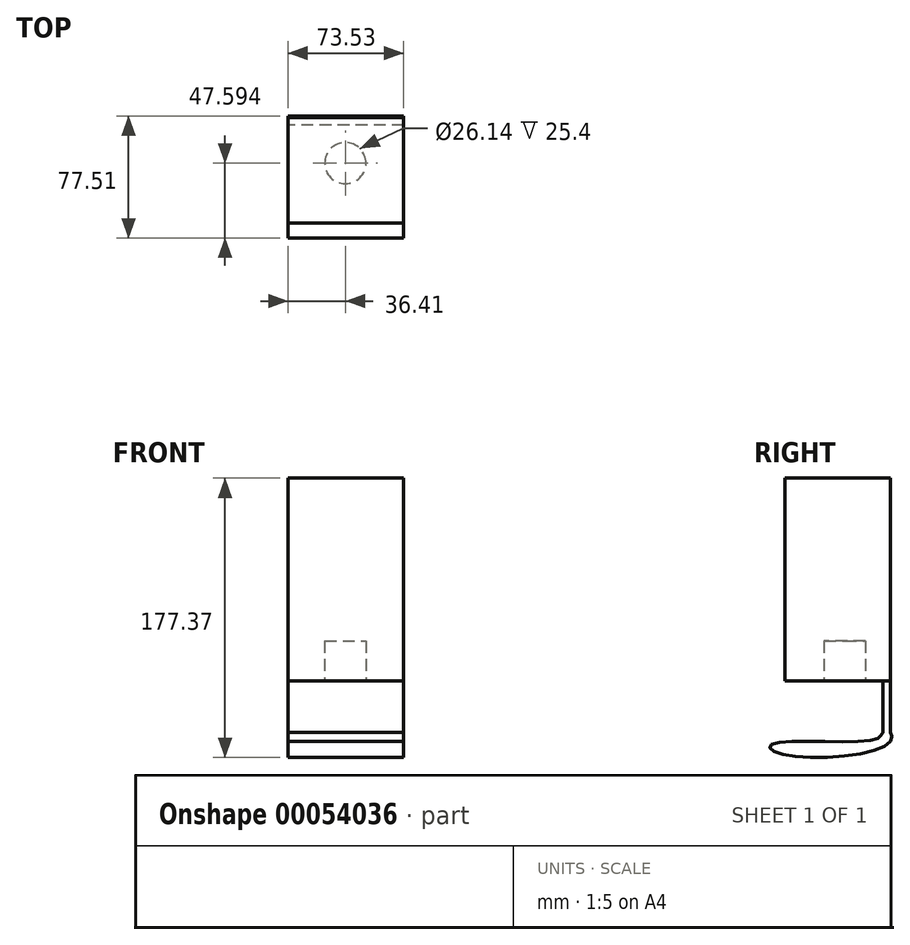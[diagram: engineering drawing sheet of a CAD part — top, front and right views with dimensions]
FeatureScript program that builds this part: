
annotation { "Feature Type Name" : "Feature", "Feature Type Description" : "" }
export const myFeature = defineFeature(function(context is Context, id is Id, definition is map)
    precondition{}
    {
        {
            var Q0;
            Q0=qCreatedBy(makeId("Front.planeOp"),FACE);
            var sketch = newSketch(context, id + "F0", { "sketchPlane" : qUnion([Q0])});
            skLineSegment(sketch, "E0.bottom", {"start": v(-36.41, 53.04) * mm, "end": v(37.08, 53.04) * mm});
            skLineSegment(sketch, "E0.top", {"start": v(-36.41, -75.77) * mm, "end": v(37.08, -75.77) * mm});
            skLineSegment(sketch, "E0.left", {"start": v(-36.41, 53.04) * mm, "end": v(-36.41, -75.77) * mm});
            skLineSegment(sketch, "E0.right", {"start": v(37.08, 53.04) * mm, "end": v(37.08, -75.77) * mm});
            skSolve(sketch);
        }
        {
            var Q0;
            Q0=makeQuery(id+"F0.imprint","IMPRINT",FACE,{"disambiguationData":[TD([[makeQuery(id+"F0.imprint","IMPRINT",EDGE,{"derivedFrom":sQuery(id+"F0.wireOp",EDGE,"E0.bottom")}),-1.0]])]});
            extrude(context, id + "F1", {"entities" : qUnion([Q0]), "depth" : 66.9 * mm});
        }
        {
            var Q0;
            Q0=makeQuery(id+"F1.opExtrude","SWEPT_FACE",FACE,{"disambiguationData":[OSD([sQuery(id+"F0.wireOp",EDGE,"E0.left")])]});
            var sketch = newSketch(context, id + "F2", { "sketchPlane" : qUnion([Q0])});
            skLineSegment(sketch, "E1", {"start": v(0, -75.77) * mm, "end": v(0, -108.53) * mm});
            skFitSpline(sketch, "E2", {"points": [v(0, -108.53) * mm, v(2.28, -116.35) * mm, v(71.97, -121.38) * mm, v(75.4, -116.12) * mm, v(8.91, -112.7) * mm, v(4.57, -108.53) * mm, v(0, -108.53) * mm]});
            skLineSegment(sketch, "E3", {"start": v(4.57, -108.53) * mm, "end": v(4.57, -75.77) * mm});
            skSolve(sketch);
        }
        {
            var Q0;
            {var subQ0=sQuery(id+"F2.wireOp",EDGE,"E1");Q0=makeQuery(id+"F2.imprint","IMPRINT",FACE,{"disambiguationData":[TD([[makeQuery(id+"F2.imprint","IMPRINT",EDGE,{"derivedFrom":subQ0}),1.0]])]});}
            var Q1;
            {var subQ0=sQuery(id+"F2.wireOp",EDGE,"E2");var subQ1=makeQuery(id+"F2.imprint","INTERSECT",VERTEX,{"derivedFrom":[sQuery(id+"F2.wireOp",EDGE,"E1"),subQ0]});Q1=makeQuery(id+"F2.imprint","IMPRINT",FACE,{"disambiguationData":[TD([[makeQuery(id+"F2.imprint","IMPRINT",EDGE,{"disambiguationData":[TD([[subQ1,-1.0]])],"derivedFrom":subQ0}),1.0]])]});}
            extrude(context, id + "F3", {"entities" : qUnion([Q0, Q1]), "oppositeDirection" : true, "depth" : 73.53 * mm});
        }
        {
            var Q0;
            Q0=makeQuery(id+"F1.opExtrude","SWEPT_FACE",FACE,{"disambiguationData":[OSD([sQuery(id+"F0.wireOp",EDGE,"E0.top")])]});
            var sketch = newSketch(context, id + "F4", { "sketchPlane" : qUnion([Q0])});
            skCircle(sketch, "E4", {"center": v(0, 28.89) * mm, "radius": 13.07 * mm});
            skSolve(sketch);
        }
        {
            var Q0;
            Q0=makeQuery(id+"F4.imprint","IMPRINT",FACE,{"disambiguationData":[TD([[makeQuery(id+"F4.imprint","IMPRINT",EDGE,{"derivedFrom":sQuery(id+"F4.wireOp",EDGE,"E4")}),1.0]])]});
            extrude(context, id + "F5", {"entities" : qUnion([Q0]), "operationType" : NewBodyOperationType.REMOVE, "oppositeDirection" : true, "depth" : 25.4 * mm});
        }
    });
